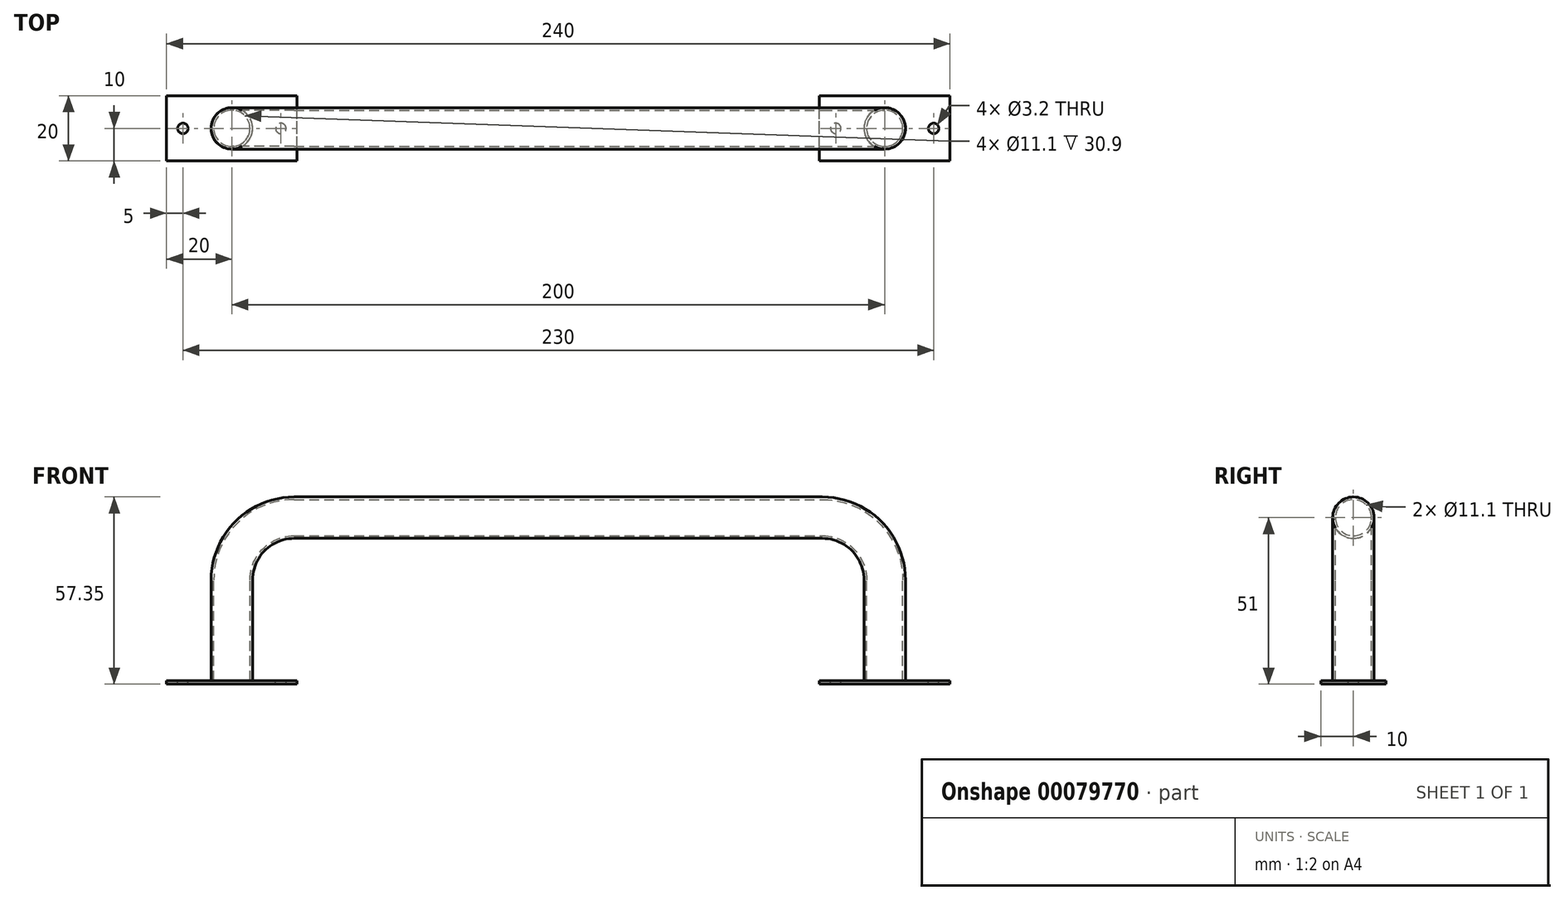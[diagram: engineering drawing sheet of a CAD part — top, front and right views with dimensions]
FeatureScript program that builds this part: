
annotation { "Feature Type Name" : "Feature", "Feature Type Description" : "" }
export const myFeature = defineFeature(function(context is Context, id is Id, definition is map)
    precondition{}
    {
        {
            var Q0;
            Q0=qCreatedBy(makeId("Top.planeOp"),FACE);
            var sketch = newSketch(context, id + "F0", { "sketchPlane" : qUnion([Q0])});
            skCircle(sketch, "E0", {"center": v(0, 0) * mm, "radius": 6.35 * mm});
            skCircle(sketch, "E1", {"center": v(0, 0) * mm, "radius": 5.55 * mm});
            skSolve(sketch);
        }
        {
            var Q0;
            Q0=qCreatedBy(makeId("Front.planeOp"),FACE);
            var sketch = newSketch(context, id + "F1", { "sketchPlane" : qUnion([Q0])});
            skLineSegment(sketch, "E2", {"start": v(0, 0) * mm, "end": v(0, 30.9) * mm});
            skLineSegment(sketch, "E3", {"start": v(19.1, 50) * mm, "end": v(100, 50) * mm});
            skPoint(sketch, "E4.visualSharp", {"position": v(0, 50) * mm});
            skArc(sketch, "E4.filletArc", {"start": v(19.1, 50) * mm, "mid": v(5.6, 44.4) * mm, "end": v(0, 30.9) * mm});
            skSolve(sketch);
        }
        {
            var Q0;
            Q0 = qSketchRegion(id + "F0", true);
            var Q1;
            Q1 = qConstructionFilter(qBodyType(qCreatedBy(id + "F1" ,EDGE), BodyType.WIRE), ConstructionObject.NO);
            sweep(context, id + "F2", {"profiles" : qUnion([Q0]), "path" : qUnion([Q1])});
        }
        {
            var Q0;
            Q0=qCreatedBy(makeId("Right.planeOp"),FACE);
            var Q1;
            Q1=sQuery(id+"F1.wireOp",VERTEX,"E3.end");
            cPlane(context, id + "F3", {"entities" : qUnion([Q0, Q1]), "cplaneType" : CPlaneType.PLANE_POINT, "offset" : 150 * mm, "width" : 150 * mm, "height" : 150 * mm});
        }
        {
            var Q0;
            Q0=qCreatedBy(makeId("Top.planeOp"),FACE);
            var sketch = newSketch(context, id + "F4", { "sketchPlane" : qUnion([Q0])});
            skLineSegment(sketch, "E5.bottom", {"start": v(20, -10) * mm, "end": v(-20, -10) * mm});
            skLineSegment(sketch, "E5.top", {"start": v(20, 10) * mm, "end": v(-20, 10) * mm});
            skLineSegment(sketch, "E5.left", {"start": v(20, -10) * mm, "end": v(20, 10) * mm});
            skLineSegment(sketch, "E5.right", {"start": v(-20, -10) * mm, "end": v(-20, 10) * mm});
            skPoint(sketch, "E5.middle", {"position": v(0, 0) * mm});
            skCircle(sketch, "E6", {"center": v(15, 0) * mm, "radius": 1.6 * mm});
            skCircle(sketch, "E7", {"center": v(-15, 0) * mm, "radius": 1.6 * mm});
            skSolve(sketch);
        }
        {
            var Q0;
            Q0 = qSketchRegion(id + "F4", true);
            extrude(context, id + "F5", {"entities" : qUnion([Q0]), "oppositeDirection" : true, "depth" : 1 * mm});
        }
        {
            var Q0;
            Q0=makeQuery(id+"F2.opSweep","SWEPT_BODY",BODY,{"disambiguationData":[OSD([sQuery(id+"F0.wireOp",EDGE,"E0"),sQuery(id+"F0.wireOp",EDGE,"E1"),sQuery(id+"F1.wireOp",EDGE,"E2")])]});
            var Q1;
            Q1=qCreatedBy(id+"F3.planeOp",FACE);
            mirror(context, id + "F6", {"operationType" : NewBodyOperationType.ADD, "entities" : qUnion([Q0]), "mirrorPlane" : qUnion([Q1])});
        }
        {
            var Q0;
            Q0=makeQuery(id+"F5.opExtrude","SWEPT_BODY",BODY,{"disambiguationData":[OSD([sQuery(id+"F4.wireOp",EDGE,"E5.bottom"),sQuery(id+"F4.wireOp",EDGE,"E5.top"),sQuery(id+"F4.wireOp",EDGE,"E5.left"),sQuery(id+"F4.wireOp",EDGE,"E5.right"),sQuery(id+"F4.wireOp",EDGE,"E6"),sQuery(id+"F4.wireOp",EDGE,"E7")])]});
            var Q1;
            Q1=qCreatedBy(id+"F3.planeOp",FACE);
            mirror(context, id + "F7", {"entities" : qUnion([Q0]), "mirrorPlane" : qUnion([Q1])});
        }
    });
